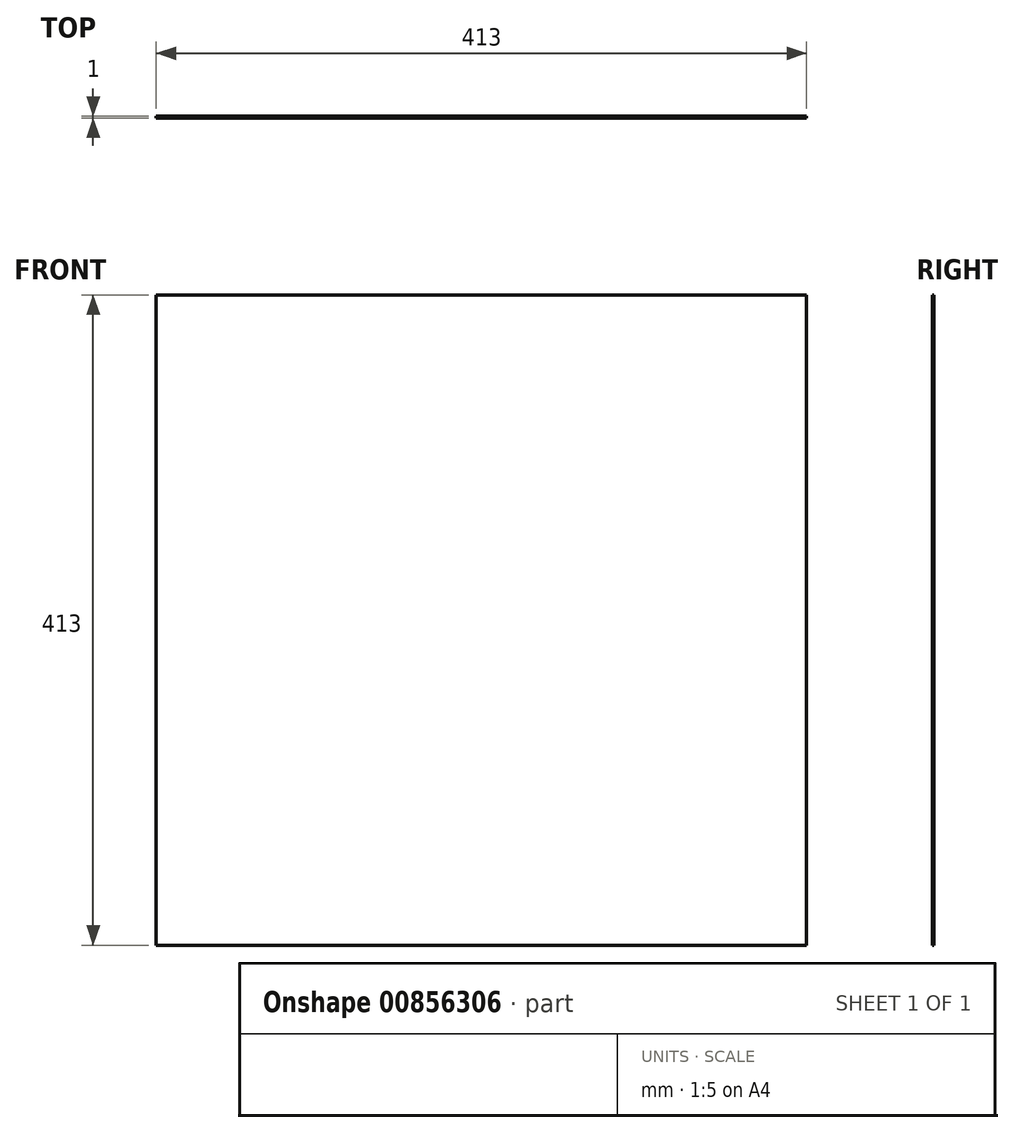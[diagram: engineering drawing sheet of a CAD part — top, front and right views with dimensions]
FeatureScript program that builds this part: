
annotation { "Feature Type Name" : "Feature", "Feature Type Description" : "" }
export const myFeature = defineFeature(function(context is Context, id is Id, definition is map)
    precondition{}
    {
        {
            var Q0;
            Q0=qCreatedBy(makeId("Front.planeOp"),FACE);
            var sketch = newSketch(context, id + "F0", { "sketchPlane" : qUnion([Q0])});
            skLineSegment(sketch, "E0", {"start": v(0, 412.48) * mm, "end": v(0, -455.2) * mm, "construction": true});
            skLineSegment(sketch, "E1", {"start": v(-487.25, 0) * mm, "end": v(516.01, 0) * mm, "construction": true});
            skLineSegment(sketch, "E2.bottom", {"start": v(-206.5, 206.5) * mm, "end": v(206.5, 206.5) * mm});
            skLineSegment(sketch, "E2.top", {"start": v(-206.5, -206.5) * mm, "end": v(206.5, -206.5) * mm});
            skLineSegment(sketch, "E2.left", {"start": v(-206.5, 206.5) * mm, "end": v(-206.5, -206.5) * mm});
            skLineSegment(sketch, "E2.right", {"start": v(206.5, 206.5) * mm, "end": v(206.5, -206.5) * mm});
            skSolve(sketch);
        }
        {
            var Q0;
            Q0 = qSketchRegion(id + "F0", true);
            extrude(context, id + "F1", {"entities" : qUnion([Q0]), "depth" : 1 * mm, "offsetDistance" : 25 * mm});
        }
    });
